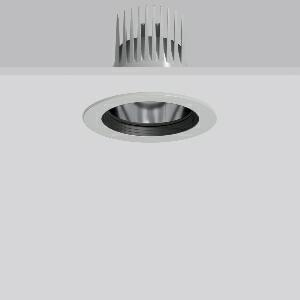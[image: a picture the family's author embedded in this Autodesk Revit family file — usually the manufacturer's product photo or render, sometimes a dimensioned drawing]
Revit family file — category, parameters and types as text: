
# Revit family: heledon_maxi_e_901765_004_3_20a1
name_source: partatom
category: Lighting Fixtures
units: mm (PartAtom-declared; Revit-internal decimal feet)

## family parameters
Cut with Voids When Loaded = No
Host = Face
Light Source = No
Part Type = Normal
Room Calculation Point = No
Round Connector Dimension = Use Diameter
Shared = No

## types (1)
- HELEDON maxi E (1 x LED Modul 935, 4400 lm, 3500)
    Apparent Load = 35 VA
    Approval mark = CE
    CIE Flux Codes = 100 100 100 100 100
    Color Rendering = 92
    Color Temperature = 3500
    Default Elevation = 1800 mm
    Description = Series: HELEDON maxi
Round recessed downlight. Housing: die-cast aluminium, powder-coated. Black plastic ring and recessed LED to prevent glare from the side. Optical assembly with reflector made of MIRO-Silver with 98% total light reflection for outstanding efficiency - can be changed without tools. Best colour rendering index Ra>90. Suitable for Recessed ceiling mounting. Installation without tools thanks to spring fastening system. Including separate LED converter with connecting cable 600 mm.High quality converter without flickering and stroboscopic effect. Through-wiring box (5 pole) available as accessory. The following accessories can be mounted without use of tools: interchangeable lenses, decorative glasses, honeycomb louvre, clear and frosted diffusers, white interchangeable plastic ring. 
Colour: silver
Diameter: 162 mm
Height: 3 mm
Cut-out diameter: 152 mm
Recess height: 200 mm
Luminaire: recess height: 135 mm
Lamp: LED
Socket: without socket
Colour temperature: 3500K
Colour rendering index (CRI): 92
System power: 35 W
Rated luminous flux: 4400 lm
Luminous efficiency: 126 lm/W
Control gear: Regulated power supply
Protection class: II
Type of protection: IP 20
    Height = 0 mm  [stored 0 ft]
    Lamp = 1 x LED Modul 935
    Lamp Light Flux = 4400 lm
    Lamp count = 1
    Length = 162 mm
    Lifetime = 50000 h
    Luminous efficacy = 126 lm/W
    Manufacturer = RZB
    ModVariant = No
    Model = 901765.004.3
    Mounting Place = Ceiling
    Mounting Type = Recessed
    Number of Poles = 1
    OnlyDefault = Yes
    Power Factor = 1
    Product Name = HELEDON maxi E
    Product group = Recessed downlights
    ProductGroupID = 402
    Protection Class = Protection class II
    Protection Degree = IP 20
    RLX_Detail_Level = 1
    RLX_Emergency_Light_Flux = 0 lm
    RLX_Emergency_Type = 0
    RLX_Emergency_Type_DB = No
    RlxData = <blob elided: 119461 chars, md5=955379bb>
    Socket = socket
    Standby Power = 0 W
    System Light Flux = 4400 lm
    System Power = 35 W
    Type Comments = Product without accessories
    Type Image = 901662.004.jpg
    URL = http://relux.com
    VarID = ---
    Voltage = 230 V
    Voltage Range = 220-240 V
    Weight = 0.00 kg
    Width = 0 mm  [stored 0 ft]

note: [stored X ft] marks values corroborated as IEEE doubles in the binary element streams (Revit-internal decimal feet)

## geometry (parser evidence)
native form markers: Blend x4, Sweep x10
no freeform markers — native parametric forms only
